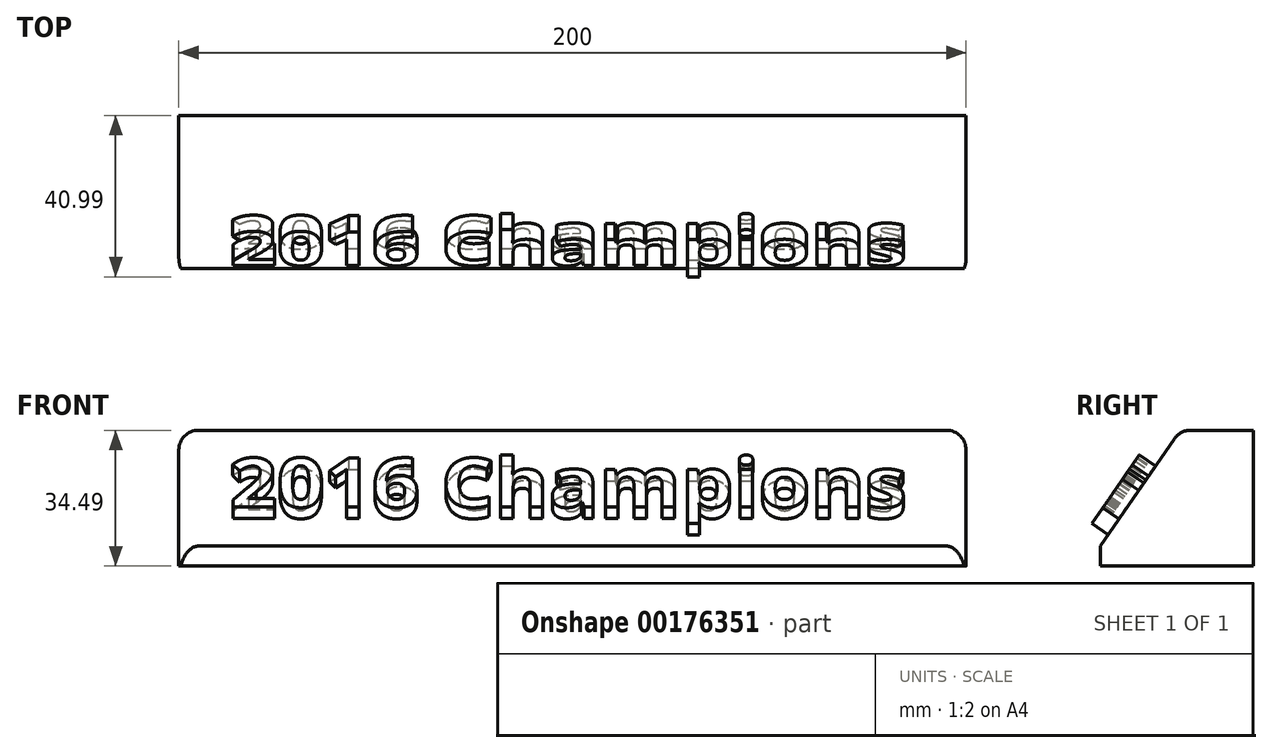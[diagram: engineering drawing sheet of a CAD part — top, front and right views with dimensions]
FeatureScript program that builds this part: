
annotation { "Feature Type Name" : "Feature", "Feature Type Description" : "" }
export const myFeature = defineFeature(function(context is Context, id is Id, definition is map)
    precondition{}
    {
        {
            var Q0;
            Q0=qCreatedBy(makeId("Right.planeOp"),FACE);
            var sketch = newSketch(context, id + "F0", { "sketchPlane" : qUnion([Q0])});
            skLineSegment(sketch, "E0", {"start": v(-27.13, -22.65) * mm, "end": v(11.73, -22.65) * mm});
            skLineSegment(sketch, "E1", {"start": v(11.73, -22.65) * mm, "end": v(11.73, 11.84) * mm});
            skLineSegment(sketch, "E2", {"start": v(11.73, 11.84) * mm, "end": v(-6.9, 11.84) * mm});
            skLineSegment(sketch, "E3", {"start": v(-6.9, 11.84) * mm, "end": v(-27.13, -17.59) * mm});
            skLineSegment(sketch, "E4", {"start": v(-27.13, -17.59) * mm, "end": v(-27.13, -22.65) * mm});
            skSolve(sketch);
        }
        {
            var Q0;
            Q0 = qSketchRegion(id + "F0", true);
            extrude(context, id + "F1", {"entities" : qUnion([Q0]), "depth" : 200 * mm});
        }
        {
            var Q0;
            Q0=makeQuery(id+"F1.opExtrude","SWEPT_FACE",FACE,{"disambiguationData":[OSD([sQuery(id+"F0.wireOp",EDGE,"E3")])]});
            var sketch = newSketch(context, id + "F2", { "sketchPlane" : qUnion([Q0])});
            skText(sketch, "E5", { "text": "2016 Champions", "fontName": "OpenSans-Bold.ttf"});
            const initialGuessF2  = {"E5": [0.01288, -0.02127, 1, 0, 0.01522]};
            skSetInitialGuess(sketch, initialGuessF2);
            skSolve(sketch);
        }
        {
            var Q0;
            Q0 = qSketchRegion(id + "F2", true);
            extrude(context, id + "F3", {"entities" : qUnion([Q0]), "operationType" : NewBodyOperationType.ADD, "depth" : 5 * mm});
        }
        {
            var Q0;
            Q0=makeQuery(id+"F1.opExtrude","SWEPT_EDGE",EDGE,{"disambiguationData":[OSD([sQuery(id+"F0.wireOp",EDGE,"E2"),sQuery(id+"F0.wireOp",EDGE,"E3")])]});
            var Q1;
            Q1=makeQuery(id+"F1.opExtrude","CAP_EDGE",EDGE,{"disambiguationData":[OSD([sQuery(id+"F0.wireOp",EDGE,"E2")])],"isStart":false});
            var Q2;
            Q2=makeQuery(id+"F1.opExtrude","CAP_EDGE",EDGE,{"disambiguationData":[OSD([sQuery(id+"F0.wireOp",EDGE,"E3")])],"isStart":false});
            var Q3;
            Q3=makeQuery(id+"F1.opExtrude","CAP_EDGE",EDGE,{"disambiguationData":[OSD([sQuery(id+"F0.wireOp",EDGE,"E2")])],"isStart":true});
            var Q4;
            Q4=makeQuery(id+"F1.opExtrude","CAP_EDGE",EDGE,{"disambiguationData":[OSD([sQuery(id+"F0.wireOp",EDGE,"E3")])],"isStart":true});
            fillet(context, id + "F4", {"entities" : qUnion([Q0, Q1, Q2, Q3, Q4]), "radius" : 5 * mm, "tangentPropagation" : true, "allowEdgeOverflow" : false});
        }
    });
